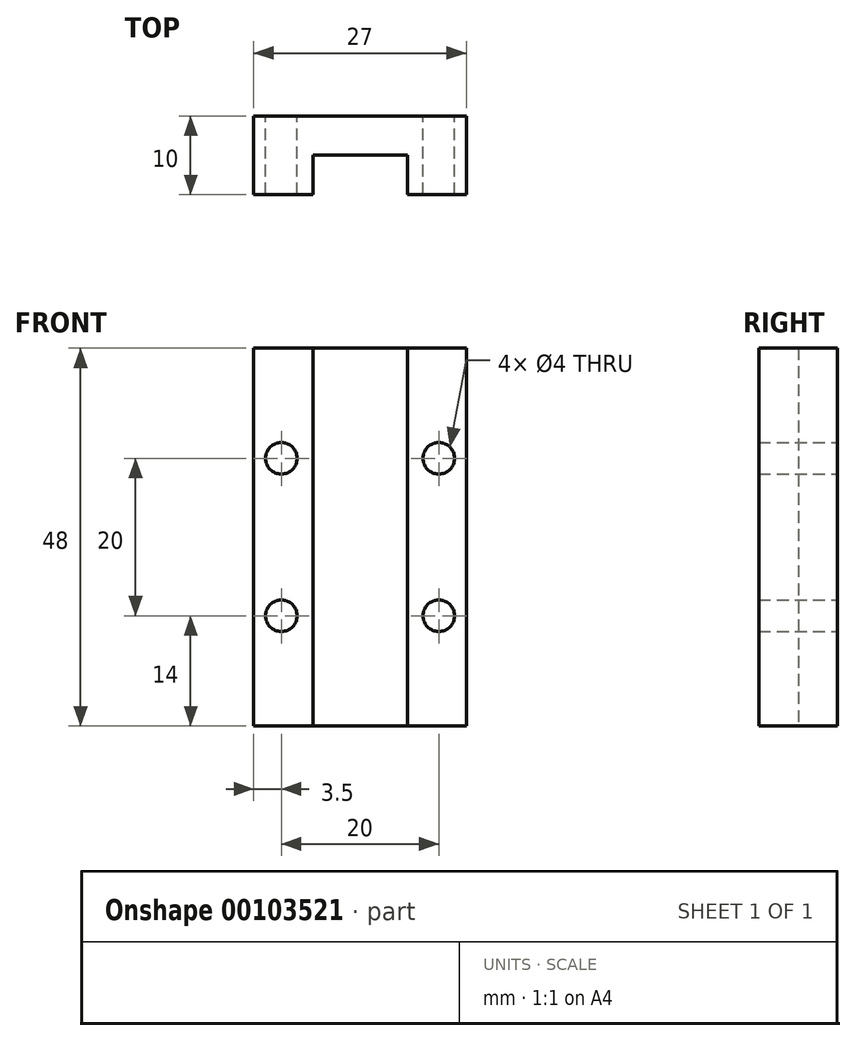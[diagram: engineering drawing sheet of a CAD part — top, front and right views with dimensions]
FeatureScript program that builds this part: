
annotation { "Feature Type Name" : "Feature", "Feature Type Description" : "" }
export const myFeature = defineFeature(function(context is Context, id is Id, definition is map)
    precondition{}
    {
        {
            var Q0;
            Q0=qCreatedBy(makeId("Top.planeOp"),FACE);
            var sketch = newSketch(context, id + "F0", { "sketchPlane" : qUnion([Q0])});
            skLineSegment(sketch, "E0.bottom", {"start": v(6, 4) * mm, "end": v(-6, 4) * mm});
            skLineSegment(sketch, "E0.top", {"start": v(6, -4) * mm, "end": v(-6, -4) * mm});
            skLineSegment(sketch, "E0.left", {"start": v(6, 4) * mm, "end": v(6, -4) * mm});
            skLineSegment(sketch, "E0.right", {"start": v(-6, 4) * mm, "end": v(-6, -4) * mm});
            skPoint(sketch, "E0.middle", {"position": v(0, 0) * mm});
            skLineSegment(sketch, "E1.bottom", {"start": v(13.5, 9) * mm, "end": v(-13.5, 9) * mm});
            skLineSegment(sketch, "E1.top", {"start": v(13.5, -1) * mm, "end": v(-13.5, -1) * mm});
            skLineSegment(sketch, "E1.left", {"start": v(13.5, 9) * mm, "end": v(13.5, -1) * mm});
            skLineSegment(sketch, "E1.right", {"start": v(-13.5, 9) * mm, "end": v(-13.5, -1) * mm});
            skPoint(sketch, "E1.middle", {"position": v(0, 4) * mm});
            skSolve(sketch);
        }
        {
            var Q0;
            {var subQ1=sQuery(id+"F0.wireOp",EDGE,"E0.bottom");Q0=makeQuery(id+"F0.imprint","IMPRINT",FACE,{"disambiguationData":[TD([[makeQuery(id+"F0.imprint","IMPRINT",EDGE,{"derivedFrom":subQ1}),-1.0]])]});}
            extrude(context, id + "F1", {"entities" : qUnion([Q0]), "depth" : 48 * mm});
        }
        {
            var Q0;
            Q0=makeQuery(id+"F1.opExtrude","SWEPT_FACE",FACE,{"disambiguationData":[OSD([sQuery(id+"F0.wireOp",EDGE,"E1.bottom")])]});
            var sketch = newSketch(context, id + "F2", { "sketchPlane" : qUnion([Q0])});
            skLineSegment(sketch, "E2", {"start": v(0, 48) * mm, "end": v(0, 0) * mm, "construction": true});
            skLineSegment(sketch, "E3.bottom", {"start": v(10, 34) * mm, "end": v(-10, 34) * mm, "construction": true});
            skLineSegment(sketch, "E3.top", {"start": v(10, 14) * mm, "end": v(-10, 14) * mm, "construction": true});
            skLineSegment(sketch, "E3.left", {"start": v(10, 34) * mm, "end": v(10, 14) * mm, "construction": true});
            skLineSegment(sketch, "E3.right", {"start": v(-10, 34) * mm, "end": v(-10, 14) * mm, "construction": true});
            skPoint(sketch, "E3.middle", {"position": v(0, 24) * mm});
            skCircle(sketch, "E4", {"center": v(-10, 34) * mm, "radius": 2 * mm});
            skCircle(sketch, "E5", {"center": v(10, 34) * mm, "radius": 2 * mm});
            skCircle(sketch, "E6", {"center": v(10, 14) * mm, "radius": 2 * mm});
            skCircle(sketch, "E7", {"center": v(-10, 14) * mm, "radius": 2 * mm});
            skSolve(sketch);
        }
        {
            var Q0;
            Q0 = qSketchRegion(id + "F2", true);
            extrude(context, id + "F3", {"entities" : qUnion([Q0]), "operationType" : NewBodyOperationType.REMOVE, "oppositeDirection" : true, "depth" : 10 * mm});
        }
    });
